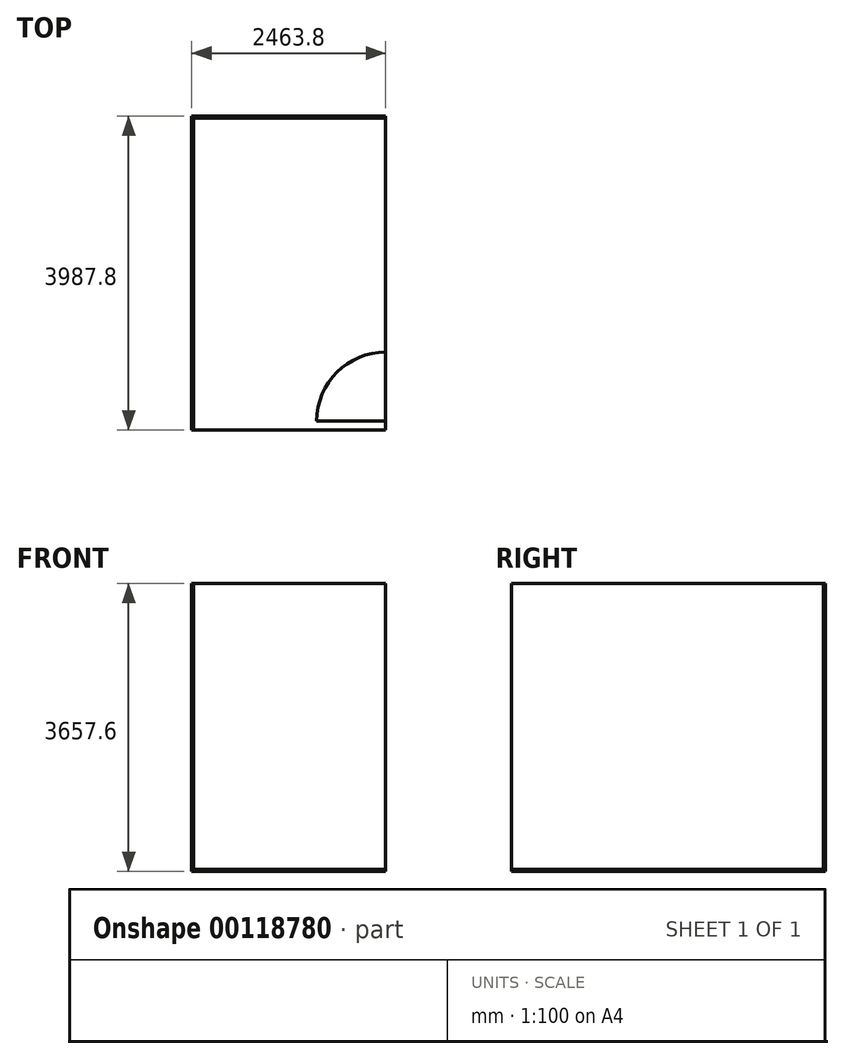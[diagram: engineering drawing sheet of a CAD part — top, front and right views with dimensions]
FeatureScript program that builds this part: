
annotation { "Feature Type Name" : "Feature", "Feature Type Description" : "" }
export const myFeature = defineFeature(function(context is Context, id is Id, definition is map)
    precondition{}
    {
        {
            var Q0;
            Q0=qCreatedBy(makeId("Top.planeOp"),FACE);
            var sketch = newSketch(context, id + "F0", { "sketchPlane" : qUnion([Q0])});
            skLineSegment(sketch, "E0.bottom", {"start": v(1231.9, -1993.9) * mm, "end": v(-1231.9, -1993.9) * mm});
            skLineSegment(sketch, "E0.top", {"start": v(1231.9, 1993.9) * mm, "end": v(-1231.9, 1993.9) * mm});
            skLineSegment(sketch, "E0.left", {"start": v(1231.9, -1993.9) * mm, "end": v(1231.9, 1993.9) * mm});
            skLineSegment(sketch, "E0.right", {"start": v(-1231.9, -1993.9) * mm, "end": v(-1231.9, 1993.9) * mm});
            skPoint(sketch, "E0.middle", {"position": v(0, 0) * mm});
            skSolve(sketch);
        }
        {
            var Q0;
            Q0 = qSketchRegion(id + "F0", true);
            extrude(context, id + "F1", {"entities" : qUnion([Q0]), "depth" : 3657.6 * mm});
        }
        {
            var Q0;
            Q0=makeQuery(id+"F1.opExtrude","CAP_FACE",FACE,{"disambiguationData":[OSD([sQuery(id+"F0.wireOp",EDGE,"E0.bottom"),sQuery(id+"F0.wireOp",EDGE,"E0.top"),sQuery(id+"F0.wireOp",EDGE,"E0.left"),sQuery(id+"F0.wireOp",EDGE,"E0.right")])],"isStart":false});
            var sketch = newSketch(context, id + "F2", { "sketchPlane" : qUnion([Q0])});
            skLineSegment(sketch, "E1", {"start": v(-1231.9, 1993.9) * mm, "end": v(-1231.9, 1968.5) * mm, "construction": true});
            skLineSegment(sketch, "E2", {"start": v(-1231.9, 1968.5) * mm, "end": v(-1206.5, 1968.5) * mm, "construction": true});
            skLineSegment(sketch, "E3.bottom", {"start": v(-1206.5, 1968.5) * mm, "end": v(2236.3, 1968.5) * mm});
            skLineSegment(sketch, "E3.top", {"start": v(-1206.5, -3038.22) * mm, "end": v(2236.3, -3038.22) * mm});
            skLineSegment(sketch, "E3.left", {"start": v(-1206.5, 1968.5) * mm, "end": v(-1206.5, -3038.22) * mm});
            skLineSegment(sketch, "E3.right", {"start": v(2236.3, 1968.5) * mm, "end": v(2236.3, -3038.22) * mm});
            skSolve(sketch);
        }
        {
            var Q0;
            Q0 = qSketchRegion(id + "F2", true);
            extrude(context, id + "F3", {"entities" : qUnion([Q0]), "operationType" : NewBodyOperationType.REMOVE, "oppositeDirection" : true, "depth" : 3632.2 * mm});
        }
        {
            var Q0;
            Q0=makeQuery(id+"F3.boolean.opBoolean","COPY",FACE,{"derivedFrom":makeQuery(id+"F3.opExtrude","CAP_FACE",FACE,{"disambiguationData":[OSD([sQuery(id+"F2.wireOp",EDGE,"E3.bottom"),sQuery(id+"F2.wireOp",EDGE,"E3.top"),sQuery(id+"F2.wireOp",EDGE,"E3.left"),sQuery(id+"F2.wireOp",EDGE,"E3.right")])],"isStart":false})});
            var sketch = newSketch(context, id + "F4", { "sketchPlane" : qUnion([Q0])});
            skLineSegment(sketch, "E4", {"start": v(1231.9, 1968.5) * mm, "end": v(1231.9, -1003.3) * mm, "construction": true});
            skLineSegment(sketch, "E5", {"start": v(1231.9, -1993.9) * mm, "end": v(1231.9, -1879.6) * mm, "construction": true});
            skLineSegment(sketch, "E6", {"start": v(1231.9, -1003.3) * mm, "end": v(1231.9, -1879.6) * mm, "construction": true});
            skLineSegment(sketch, "E7", {"start": v(1231.9, -1879.6) * mm, "end": v(355.6, -1879.6) * mm, "construction": true});
            skLineSegment(sketch, "E8", {"start": v(355.6, -1879.6) * mm, "end": v(1231.9, -1879.6) * mm});
            skLineSegment(sketch, "E9", {"start": v(1231.9, -1879.6) * mm, "end": v(1231.9, -1003.3) * mm});
            skLineSegment(sketch, "E10", {"start": v(1231.9, -1879.6) * mm, "end": v(612.26, -1259.96) * mm, "construction": true});
            skArc(sketch, "E11", {"start": v(1231.9, -1003.3) * mm, "mid": v(612.26, -1259.96) * mm, "end": v(355.6, -1879.6) * mm});
            skSolve(sketch);
        }
        {
            var Q0;
            Q0 = qSketchRegion(id + "F4", true);
            extrude(context, id + "F5", {"entities" : qUnion([Q0]), "operationType" : NewBodyOperationType.ADD, "depth" : 0.5 * mm});
        }
    });
